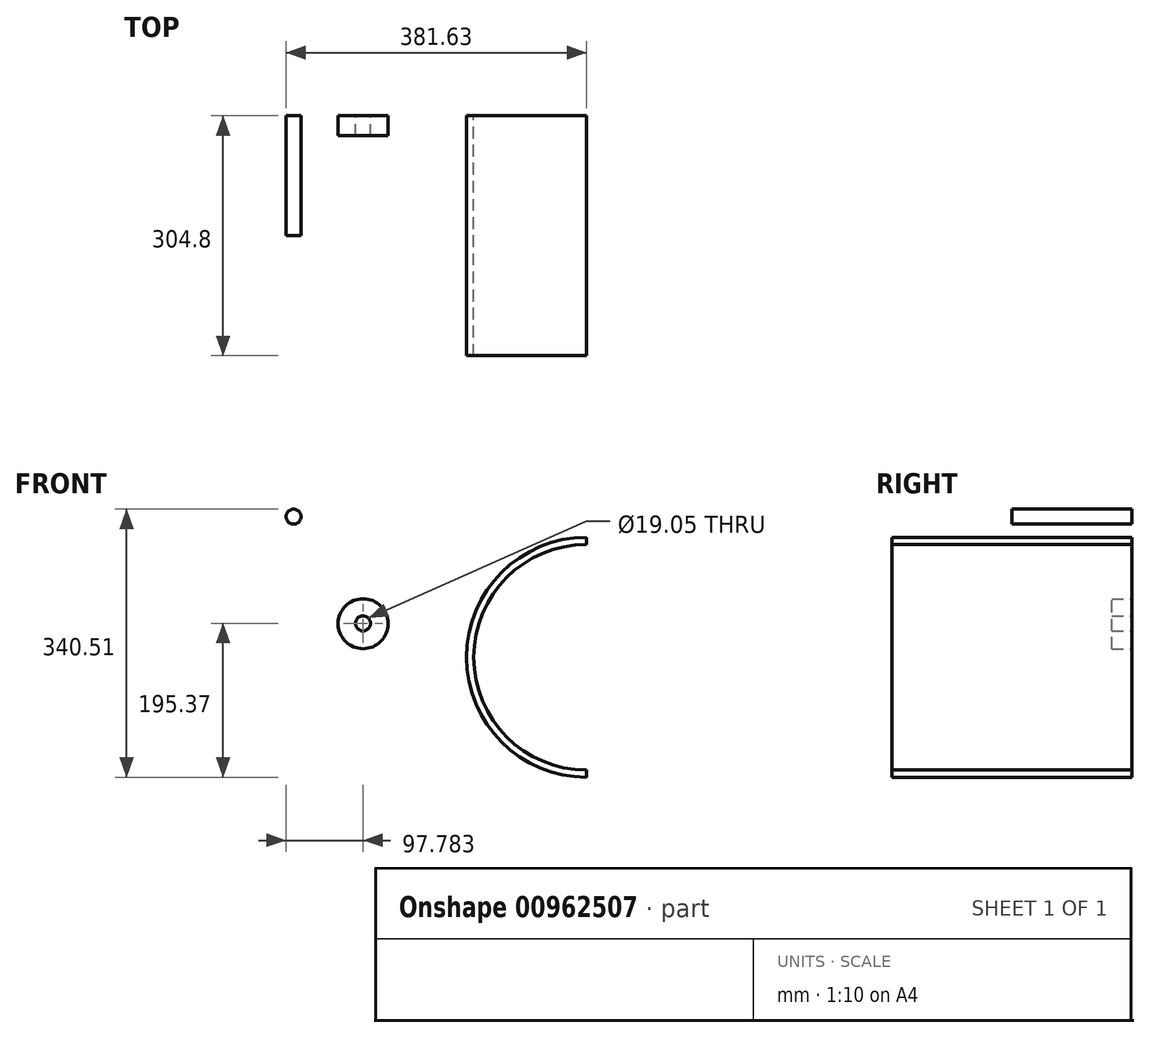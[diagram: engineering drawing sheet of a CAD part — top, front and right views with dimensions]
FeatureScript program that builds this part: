
annotation { "Feature Type Name" : "Feature", "Feature Type Description" : "" }
export const myFeature = defineFeature(function(context is Context, id is Id, definition is map)
    precondition{}
    {
        {
            var Q0;
            Q0=qCreatedBy(makeId("Front.planeOp"),FACE);
            var sketch = newSketch(context, id + "F0", { "sketchPlane" : qUnion([Q0])});
            skCircle(sketch, "E0", {"center": v(0, 0) * mm, "radius": 152.4 * mm});
            skLineSegment(sketch, "E1", {"start": v(0, -152.4) * mm, "end": v(0, 152.4) * mm});
            skSolve(sketch);
        }
        {
            var Q0;
            {var subQ0=sQuery(id+"F0.wireOp",EDGE,"E1");Q0=makeQuery(id+"F0.imprint","IMPRINT",FACE,{"disambiguationData":[TD([[makeQuery(id+"F0.imprint","IMPRINT",EDGE,{"derivedFrom":subQ0}),1.0]])]});}
            extrude(context, id + "F1", {"entities" : qUnion([Q0]), "depth" : 304.8 * mm, "offsetDistance" : 25.4 * mm});
        }
        {
            var Q0;
            Q0=qCreatedBy(makeId("Front.planeOp"),FACE);
            var sketch = newSketch(context, id + "F2", { "sketchPlane" : qUnion([Q0])});
            skCircle(sketch, "E2", {"center": v(0, 0) * mm, "radius": 143.24 * mm});
            skSolve(sketch);
        }
        {
            var Q0;
            Q0=makeQuery(id+"F2.imprint","IMPRINT",FACE,{"disambiguationData":[TD([[makeQuery(id+"F2.imprint","IMPRINT",EDGE,{"derivedFrom":sQuery(id+"F2.wireOp",EDGE,"E2")}),1.0]])]});
            extrude(context, id + "F3", {"entities" : qUnion([Q0]), "operationType" : NewBodyOperationType.REMOVE, "depth" : 304.8 * mm, "offsetDistance" : 25.4 * mm});
        }
        {
            var Q0;
            Q0=qCreatedBy(makeId("Front.planeOp"),FACE);
            var sketch = newSketch(context, id + "F4", { "sketchPlane" : qUnion([Q0])});
            skCircle(sketch, "E3", {"center": v(-372.1, 178.58) * mm, "radius": 9.53 * mm});
            skSolve(sketch);
        }
        {
            var Q0;
            Q0 = qSketchRegion(id + "F4", true);
            extrude(context, id + "F5", {"entities" : qUnion([Q0]), "depth" : 152.4 * mm, "offsetDistance" : 25.4 * mm});
        }
        {
            var Q0;
            Q0=qCreatedBy(makeId("Front.planeOp"),FACE);
            var sketch = newSketch(context, id + "F6", { "sketchPlane" : qUnion([Q0])});
            skCircle(sketch, "E4", {"center": v(-283.78, 42.6) * mm, "radius": 31.75 * mm});
            skSolve(sketch);
        }
        {
            var Q0;
            Q0=makeQuery(id+"F6.imprint","IMPRINT",FACE,{"disambiguationData":[TD([[makeQuery(id+"F6.imprint","IMPRINT",EDGE,{"derivedFrom":sQuery(id+"F6.wireOp",EDGE,"E4")}),1.0]])]});
            extrude(context, id + "F7", {"entities" : qUnion([Q0]), "depth" : 25.4 * mm, "offsetDistance" : 25.4 * mm});
        }
        {
            var Q0;
            Q0=qCreatedBy(makeId("Front.planeOp"),FACE);
            var sketch = newSketch(context, id + "F8", { "sketchPlane" : qUnion([Q0])});
            skCircle(sketch, "E5", {"center": v(-283.85, 42.97) * mm, "radius": 9.53 * mm});
            skSolve(sketch);
        }
        {
            var Q0;
            Q0=makeQuery(id+"F8.imprint","IMPRINT",FACE,{"disambiguationData":[TD([[makeQuery(id+"F8.imprint","IMPRINT",EDGE,{"derivedFrom":sQuery(id+"F8.wireOp",EDGE,"E5")}),1.0]])]});
            extrude(context, id + "F9", {"entities" : qUnion([Q0]), "operationType" : NewBodyOperationType.REMOVE, "depth" : 25.4 * mm, "offsetDistance" : 25.4 * mm});
        }
    });
